# Revit family: Kessel 48928M en
name_source: partatom
category: Sanitärinstallationen
revit_build: Autodesk Revit 2017 (Build: 20160225_1515(x64)
units: mm (PartAtom-declared; Revit-internal decimal feet)

## family parameters
Arbeitsebenenbasiert = Nein
Beim Laden mit Abzugskörper schneiden = Nein
Bemaßung runder Anschluss = Durchmesser verwenden
Gemeinsam genutzt = Nein
Immer vertikal = Ja
Raumberechnungspunkt = Nein
Teiletyp = Normal

## types (1)
- Kessel 48928M en
    <1.010.00.2> Number of the part of the guideline = 38
    <1.010.00.3> Issue date (month) of the guideline = 201805
    <1.010.00.4> Manufacturer name = Kessel
    <1.010.00.5> Revision date of the file = 20190228
    <1.800.00.3> BS number = 001039000100001000002000001???0000001000010000000100000001
    <1.800.00.4> Comment field = Aufsatzstück Linearis Comfort L: 750 mm, befestigte Dichtmanschette
    <1.810.00.3> Manufacturer’s reference number = 48928M
    <1.810.00.4> DATANORM number = 48928M
    <1.960/3L.00.8> Link (URL) = http://www.kessel.de
    <38.100.00.4> Drain type for floor, roof and sanitary objects = Bodenabläufe mit Geruchsverschluss
    <38.110.00.4> Floor, roof and sanitary works sequences = Aufsatzstück Linearis Comfort
    <38.200.00.3> Drain socket variation = -
    <38.250.00.3> Drainage type = Freispiegel
    <38.300.00.3> Type of drains for floor, roof and roofing objects = Ablauf-Linienförmig (z.B. Rinne)
    <38.360.00.3> Trace heating of the drain for floor, roof and sanitary objects = ohne Begleitheizung
    <38.500.00.3> Sealing variantion = -
    <38.550.00.3> Trap = mit Geruchverschluss
    <38.700.00.15> Connection to GLT, GA = no
    <38.700.00.16> Fire resistance class can be retrofitted = yes
    <38.700.00.18> Load class Drains, covers and attachments = K 3
    <38.700.00.4> product name = Aufsatzstück Linearis Comfort L: 750 mm, befestigte Dichtmanschette
    <38.700.00.6> Complete article (one-piece) from combination (multi-part design) Drain body and attachment piece = no
    <38.700.00.7> Potential compensation (ground connection) available = no
    <38.700.00.8> Electrical connection = no
    <38.710.01.10> depth [mm] = 243
    <38.710.01.11> installation height [mm] = 110
    <38.710.01.12> Water trap [mm] = 50
    <38.710.01.14> with sound decoupling = no
    <38.710.01.15> Leafy / Kiefang = no
    <38.710.01.3> Product name = Aufsatzstück Linearis Comfort L: 750 mm, befestigte Dichtmanschette
    <38.710.01.4> Type = floor drain
    <38.710.01.5> Nominal system = DN
    <38.710.01.6> Nominal dimensions = 125
    <38.710.01.7> Nominal pressure system = PN
    <38.710.01.8> nominal pressure = 1
    <38.710.01.9> installation width [mm] = 816
    <38.710.11.3> drainage capacity [l/s] = 1.1
    <38.710.11.4> Water level difference (accumulation height) [mm] = 10
    <38.710.12.11> Sealing frame [mm] = clamping flange
    <38.710.12.12> Rust included [mm] = no
    <38.710.12.3> Product name = Aufsatzstück Linearis Comfort L: 750 mm, befestigte Dichtmanschette
    <38.710.12.6> Material of the attachment pieces = plastic
    <38.710.12.7> Shape = rectangular
    <38.710.12.8> Length frame = 750
    <38.710.12.9> Wide frame [mm] = 66
    <38.710.13.3> Product name = Aufsatzstück Linearis Comfort L: 750 mm, befestigte Dichtmanschette
    <38.710.13.4> Variant of the drainage drain = point drain
    <38.710.13.5> Type gutter = rechteckig
    <38.710.13.7> Leafy / Kiefang = no
    <38.710.14.10> Rust included = yes
    <38.710.14.3> Product name = Aufsatzstück Linearis Comfort L: 750 mm, befestigte Dichtmanschette
    <38.710.15.10> Load class Drains, covers and attachments = K 3
    <38.710.15.3> Product name = Edelstahl-Abdeckung, Edelstahl V2A
    <38.710.15.4> Execution drain grate = Edelstahl-Abdeckung
    <38.710.15.5> Material of the drain grate = Stainless steel
    <38.710.15.6> Fixing the grate = loosely inserted
    <38.710.15.7> Execution of the drain grate = Edelstahl-Abdeckung
    <38.710.15.8> Surface drain grate = gebürstet
    <38.710.15.9> Slip resistance of the drain grate = no
    CONNECTOR0_DIAMETER_dZ_0r = 0 mm  [stored 0 ft]
    CONNECTOR0_dZ_00 = 25 mm  [stored 0.082021 ft]
    CONNECTOR0_ref_dZ = 25 mm  [stored 0.082021 ft]
    CONNECTOR1_DIAMETER_dZ_0r = 0 mm  [stored 0 ft]
    CONNECTOR1_dZ_00 = 131 mm
    CONNECTOR1_dZ_01 = 106 mm
    CONNECTOR1_ref_dZ = 106 mm
    Hersteller = Kessel
    Modell = 48928M
    URL = www.kessel.de

note: [stored X ft] marks values corroborated as IEEE doubles in the binary element streams (Revit-internal decimal feet)

## geometry (parser evidence)
native form markers: Sweep x1
no freeform markers — native parametric forms only
